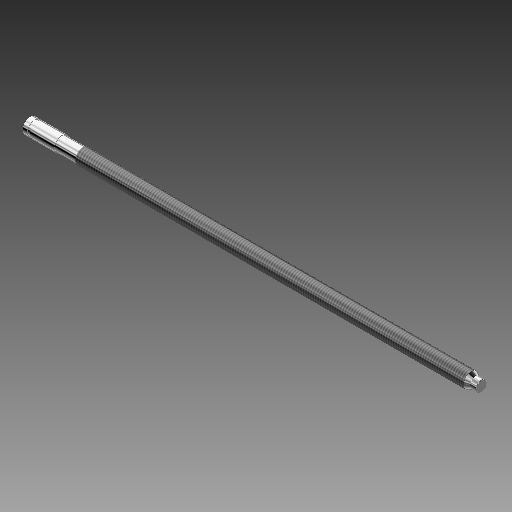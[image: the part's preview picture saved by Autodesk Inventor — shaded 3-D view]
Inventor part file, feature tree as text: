
AUTODESK INVENTOR PART (.ipt)
format: ipt  version: 2019 (Build 230136000, 136)  size: 120,320 bytes
history: native  units: mm
features: chamfer x2, revolve x1, thread x1, sketch x1
ambient origin geometry x8: Origin, YZ Plane, XZ Plane, XY Plane, X Axis, Y Axis, Z Axis, Center Point
bodies: Solid1 (feature_tree)
feature tree (5):
  revolve  "Revolution1"  [1 undecoded]
  chamfer  "Chamfer1"  Distance=17.5mm
  chamfer  "Chamfer2"  Distance=2.0mm
  thread  "Thread1"  [1 undecoded]
  sketch  "Sketch1"  dims[d0=37.75mm d1=15.0mm d2=17.5mm d3=2.0mm d4=11.06mm d5=0.5mm d6=0.5mm d7=320.0mm d8=324.5mm d9=8.0mm d10=90.0deg d11=1.53mm d12=3.0mm d13=45.0deg d14=0.5mm d15=3.0mm d16=45.0deg d17=10.0mm d18=0.0mm]
note: 2 required parameter values undecoded (feature->parameter linkage not recoverable at this tier; creation-order binding heuristic only, values carry confidence <= 0.55)